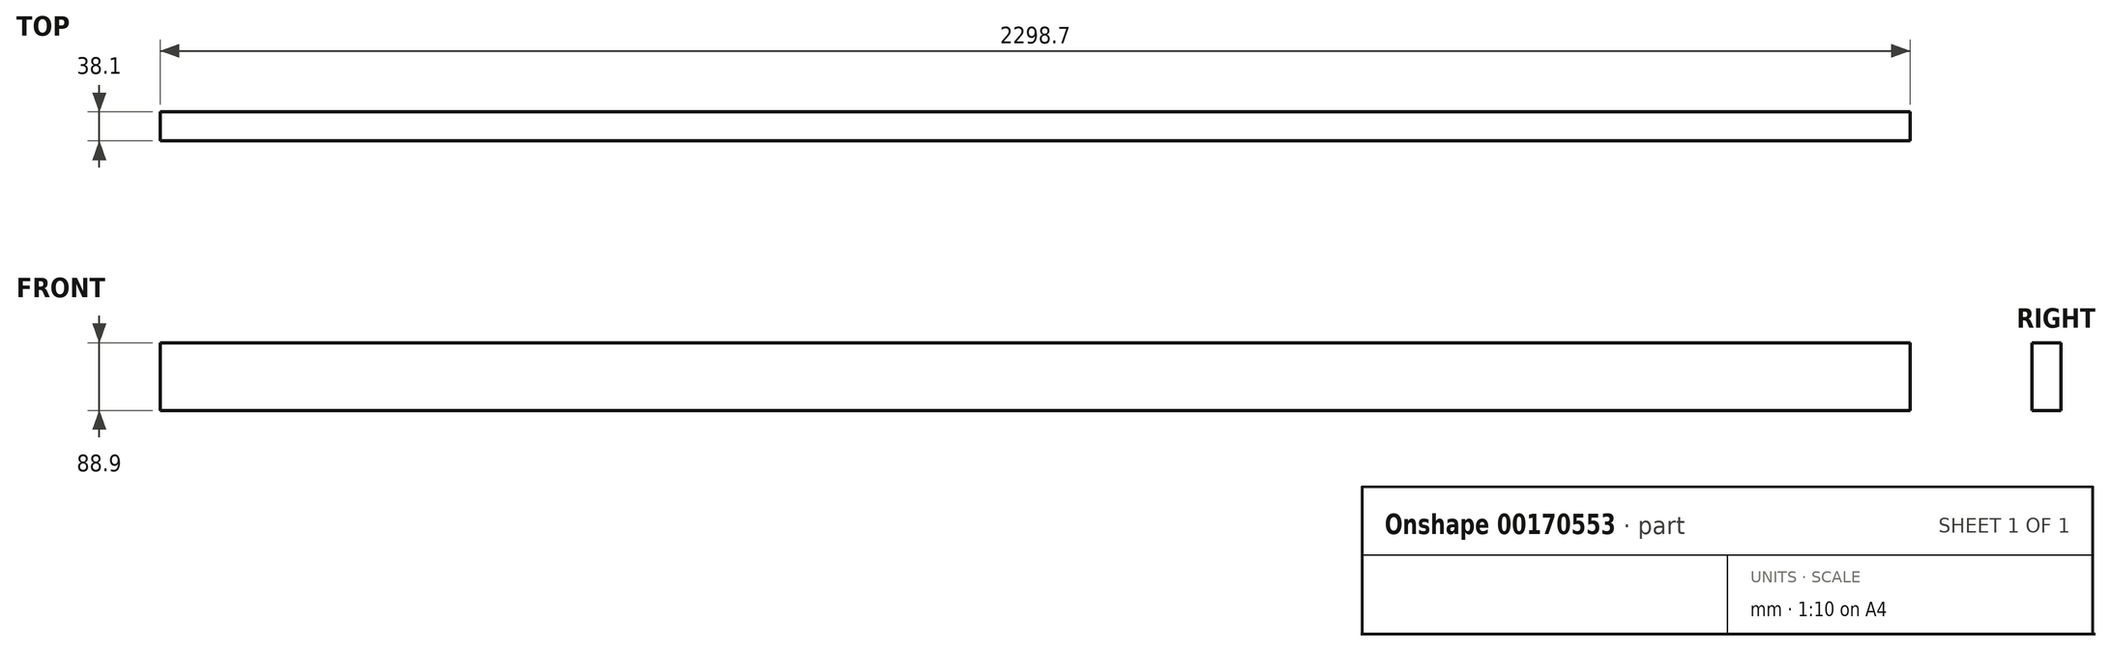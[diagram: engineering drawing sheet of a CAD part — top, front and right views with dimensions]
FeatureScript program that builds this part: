
annotation { "Feature Type Name" : "Feature", "Feature Type Description" : "" }
export const myFeature = defineFeature(function(context is Context, id is Id, definition is map)
    precondition{}
    {
        {
            var Q0;
            Q0=qCreatedBy(makeId("Right.planeOp"),FACE);
            var sketch = newSketch(context, id + "F0", { "sketchPlane" : qUnion([Q0])});
            skLineSegment(sketch, "E0.bottom", {"start": v(0, 0) * mm, "end": v(38.1, 0) * mm});
            skLineSegment(sketch, "E0.top", {"start": v(0, 88.9) * mm, "end": v(38.1, 88.9) * mm});
            skLineSegment(sketch, "E0.left", {"start": v(0, 0) * mm, "end": v(0, 88.9) * mm});
            skLineSegment(sketch, "E0.right", {"start": v(38.1, 0) * mm, "end": v(38.1, 88.9) * mm});
            skSolve(sketch);
        }
        {
            var Q0;
            Q0=makeQuery(id+"F0.imprint","IMPRINT",FACE,{"disambiguationData":[TD([[makeQuery(id+"F0.imprint","IMPRINT",EDGE,{"derivedFrom":sQuery(id+"F0.wireOp",EDGE,"E0.bottom")}),1.0]])]});
            extrude(context, id + "F1", {"entities" : qUnion([Q0]), "depth" : 2298.7 * mm});
        }
    });
